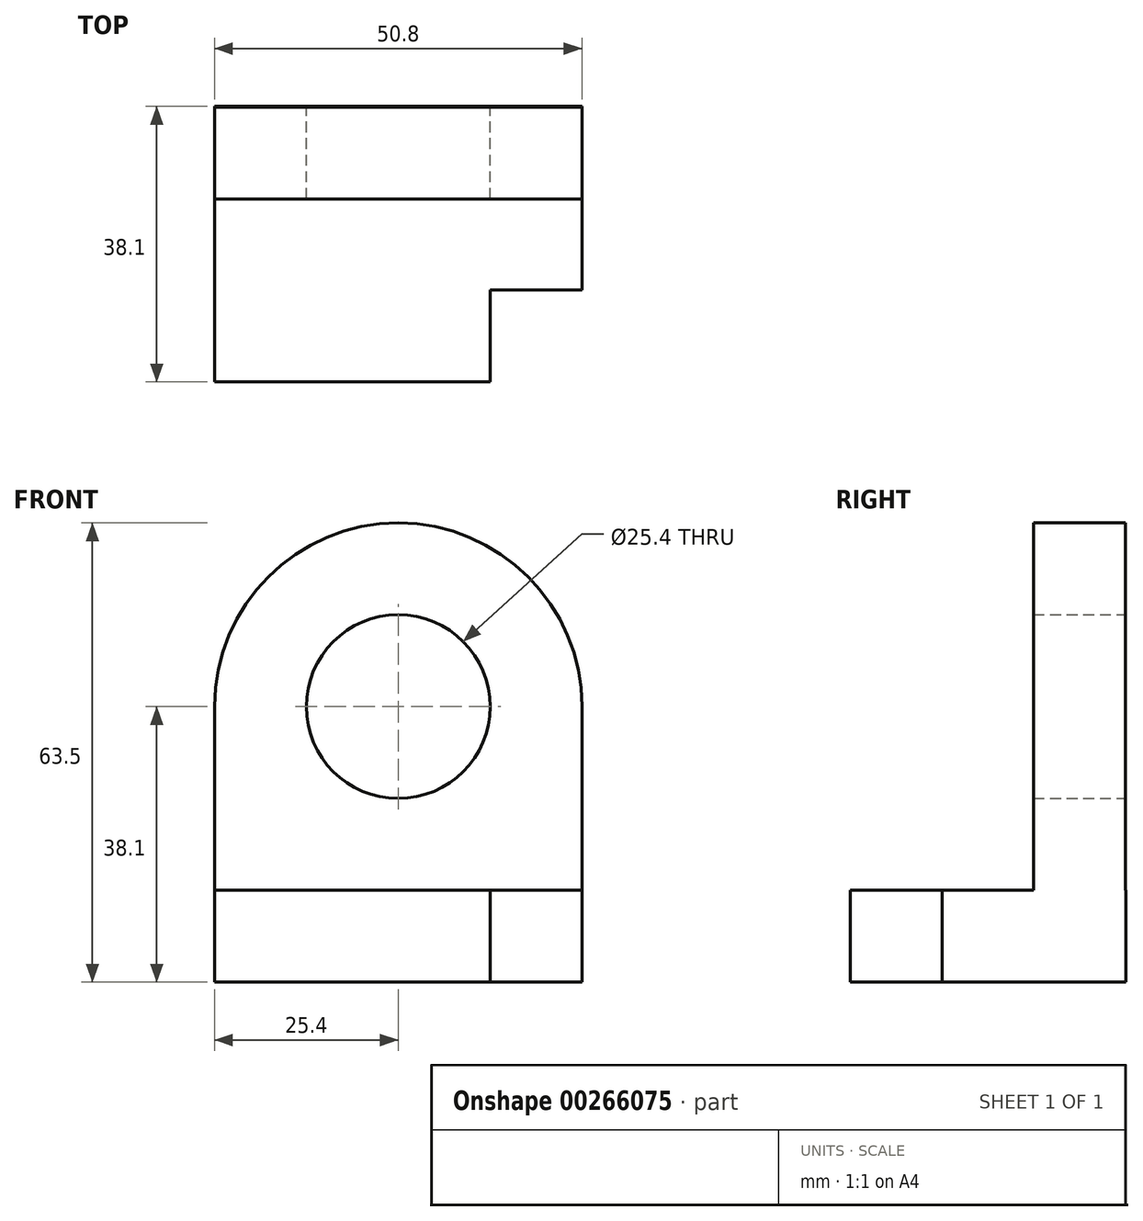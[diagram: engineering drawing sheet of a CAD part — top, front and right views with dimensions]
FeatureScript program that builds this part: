
annotation { "Feature Type Name" : "Feature", "Feature Type Description" : "" }
export const myFeature = defineFeature(function(context is Context, id is Id, definition is map)
    precondition{}
    {
        {
            var Q0;
            Q0=qCreatedBy(makeId("Top.planeOp"),FACE);
            var sketch = newSketch(context, id + "F0", { "sketchPlane" : qUnion([Q0])});
            skLineSegment(sketch, "E0.bottom", {"start": v(-25.4, 19.05) * mm, "end": v(25.4, 19.05) * mm});
            skLineSegment(sketch, "E0.top", {"start": v(-25.4, -19.05) * mm, "end": v(25.4, -19.05) * mm});
            skLineSegment(sketch, "E0.left", {"start": v(-25.4, 19.05) * mm, "end": v(-25.4, -19.05) * mm});
            skLineSegment(sketch, "E0.right", {"start": v(25.4, 19.05) * mm, "end": v(25.4, -19.05) * mm});
            skSolve(sketch);
        }
        {
            var Q0;
            Q0 = qSketchRegion(id + "F0", true);
            extrude(context, id + "F1", {"entities" : qUnion([Q0]), "depth" : 12.7 * mm});
        }
        {
            var Q0;
            Q0=makeQuery(id+"F1.opExtrude","SWEPT_FACE",FACE,{"disambiguationData":[OSD([sQuery(id+"F0.wireOp",EDGE,"E0.top")])]});
            var sketch = newSketch(context, id + "F2", { "sketchPlane" : qUnion([Q0])});
            skLineSegment(sketch, "E1.bottom", {"start": v(12.7, 12.7) * mm, "end": v(25.4, 12.7) * mm});
            skLineSegment(sketch, "E1.top", {"start": v(12.7, 0) * mm, "end": v(25.4, 0) * mm});
            skLineSegment(sketch, "E1.left", {"start": v(12.7, 12.7) * mm, "end": v(12.7, 0) * mm});
            skLineSegment(sketch, "E1.right", {"start": v(25.4, 12.7) * mm, "end": v(25.4, 0) * mm});
            skSolve(sketch);
        }
        {
            var Q0;
            Q0=makeQuery(id+"F2.imprint","IMPRINT",FACE,{"disambiguationData":[TD([[makeQuery(id+"F2.imprint","IMPRINT",EDGE,{"derivedFrom":sQuery(id+"F2.wireOp",EDGE,"E1.bottom")}),-1.0]])]});
            extrude(context, id + "F3", {"entities" : qUnion([Q0]), "operationType" : NewBodyOperationType.REMOVE, "oppositeDirection" : true, "depth" : 12.7 * mm});
        }
        {
            var Q0;
            Q0=makeQuery(id+"F1.opExtrude","SWEPT_FACE",FACE,{"disambiguationData":[OSD([sQuery(id+"F0.wireOp",EDGE,"E0.left")])]});
            var sketch = newSketch(context, id + "F4", { "sketchPlane" : qUnion([Q0])});
            skLineSegment(sketch, "E2.bottom", {"start": v(-18.96, 63.5) * mm, "end": v(-6.26, 63.5) * mm});
            skLineSegment(sketch, "E2.top", {"start": v(-18.96, 12.7) * mm, "end": v(-6.26, 12.7) * mm});
            skLineSegment(sketch, "E2.left", {"start": v(-18.96, 63.5) * mm, "end": v(-18.96, 12.7) * mm});
            skLineSegment(sketch, "E2.right", {"start": v(-6.26, 63.5) * mm, "end": v(-6.26, 12.7) * mm});
            skSolve(sketch);
        }
        {
            var Q0;
            Q0=makeQuery(id+"F4.imprint","IMPRINT",FACE,{"disambiguationData":[TD([[makeQuery(id+"F4.imprint","IMPRINT",EDGE,{"derivedFrom":sQuery(id+"F4.wireOp",EDGE,"E2.bottom")}),-1.0]])]});
            extrude(context, id + "F5", {"entities" : qUnion([Q0]), "operationType" : NewBodyOperationType.ADD, "oppositeDirection" : true, "depth" : 50.8 * mm});
        }
        {
            var Q0;
            Q0=makeQuery(id+"F5.opExtrude","SWEPT_FACE",FACE,{"disambiguationData":[OSD([sQuery(id+"F4.wireOp",EDGE,"E2.left")])]});
            var sketch = newSketch(context, id + "F6", { "sketchPlane" : qUnion([Q0])});
            skCircle(sketch, "E3", {"center": v(0, 38.1) * mm, "radius": 12.7 * mm});
            skSolve(sketch);
        }
        {
            var Q0;
            Q0 = qSketchRegion(id + "F6", true);
            extrude(context, id + "F7", {"entities" : qUnion([Q0]), "operationType" : NewBodyOperationType.REMOVE, "oppositeDirection" : true, "depth" : 12.7 * mm});
        }
        {
            var Q0;
            Q0=makeQuery(id+"F5.opExtrude","CAP_EDGE",EDGE,{"disambiguationData":[OSD([sQuery(id+"F4.wireOp",EDGE,"E2.bottom")])],"isStart":true});
            fillet(context, id + "F8", {"entities" : qUnion([Q0]), "radius" : 25.4 * mm, "tangentPropagation" : true, "allowEdgeOverflow" : false});
        }
        {
            var Q0;
            Q0=makeQuery(id+"F5.opExtrude","CAP_EDGE",EDGE,{"disambiguationData":[OSD([sQuery(id+"F4.wireOp",EDGE,"E2.bottom")])],"isStart":false});
            fillet(context, id + "F9", {"entities" : qUnion([Q0]), "radius" : 25.4 * mm, "tangentPropagation" : true, "allowEdgeOverflow" : false});
        }
    });
